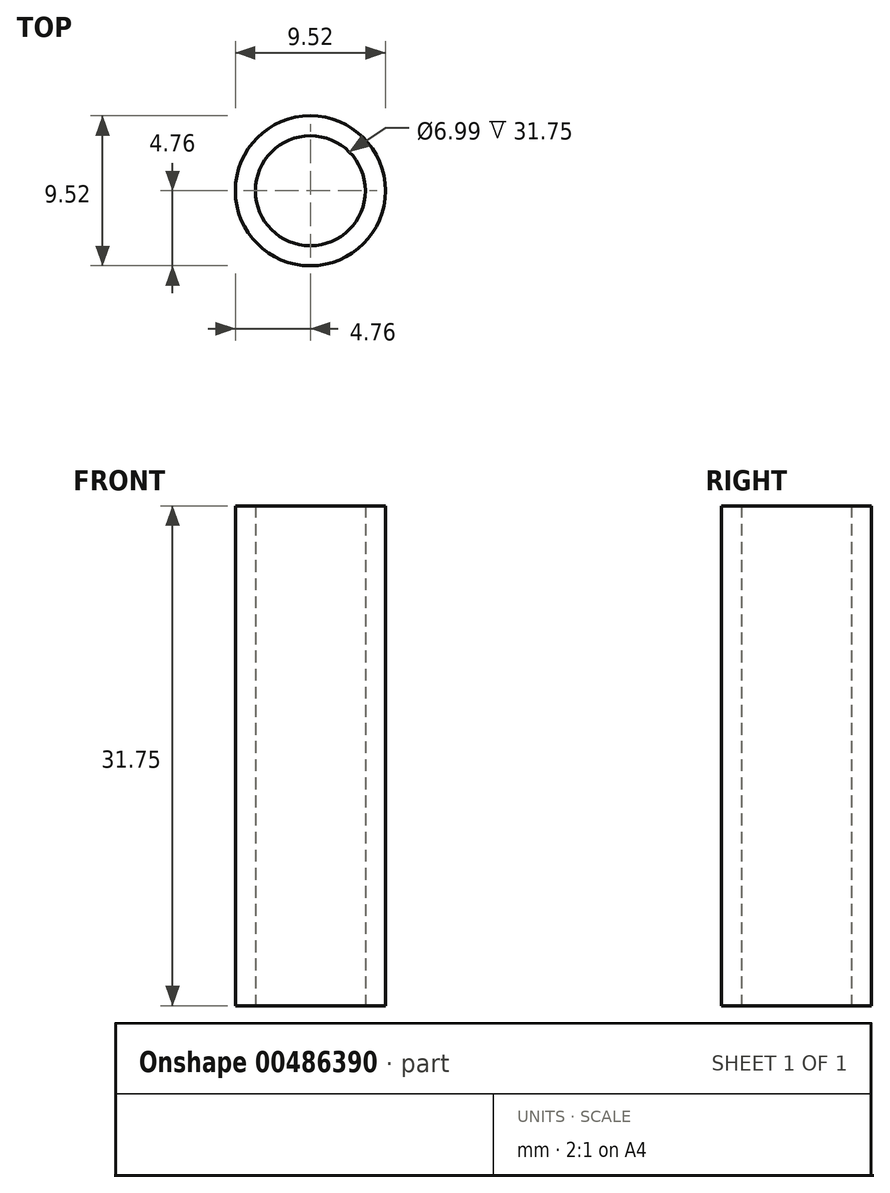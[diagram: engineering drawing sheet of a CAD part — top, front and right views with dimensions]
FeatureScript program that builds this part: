
annotation { "Feature Type Name" : "Feature", "Feature Type Description" : "" }
export const myFeature = defineFeature(function(context is Context, id is Id, definition is map)
    precondition{}
    {
        {
            var Q0;
            Q0=qCreatedBy(makeId("Top.planeOp"),FACE);
            var sketch = newSketch(context, id + "F0", { "sketchPlane" : qUnion([Q0])});
            skCircle(sketch, "E0", {"center": v(0, 0) * mm, "radius": 4.76 * mm});
            skCircle(sketch, "E1", {"center": v(0, 0) * mm, "radius": 3.5 * mm});
            skSolve(sketch);
        }
        {
            var Q0;
            Q0=makeQuery(id+"F0.imprint","IMPRINT",FACE,{"disambiguationData":[TD([[makeQuery(id+"F0.imprint","IMPRINT",EDGE,{"derivedFrom":sQuery(id+"F0.wireOp",EDGE,"E0")}),1.0]])]});
            extrude(context, id + "F1", {"entities" : qUnion([Q0]), "depth" : 31.75 * mm, "offsetDistance" : 25.4 * mm});
        }
    });
